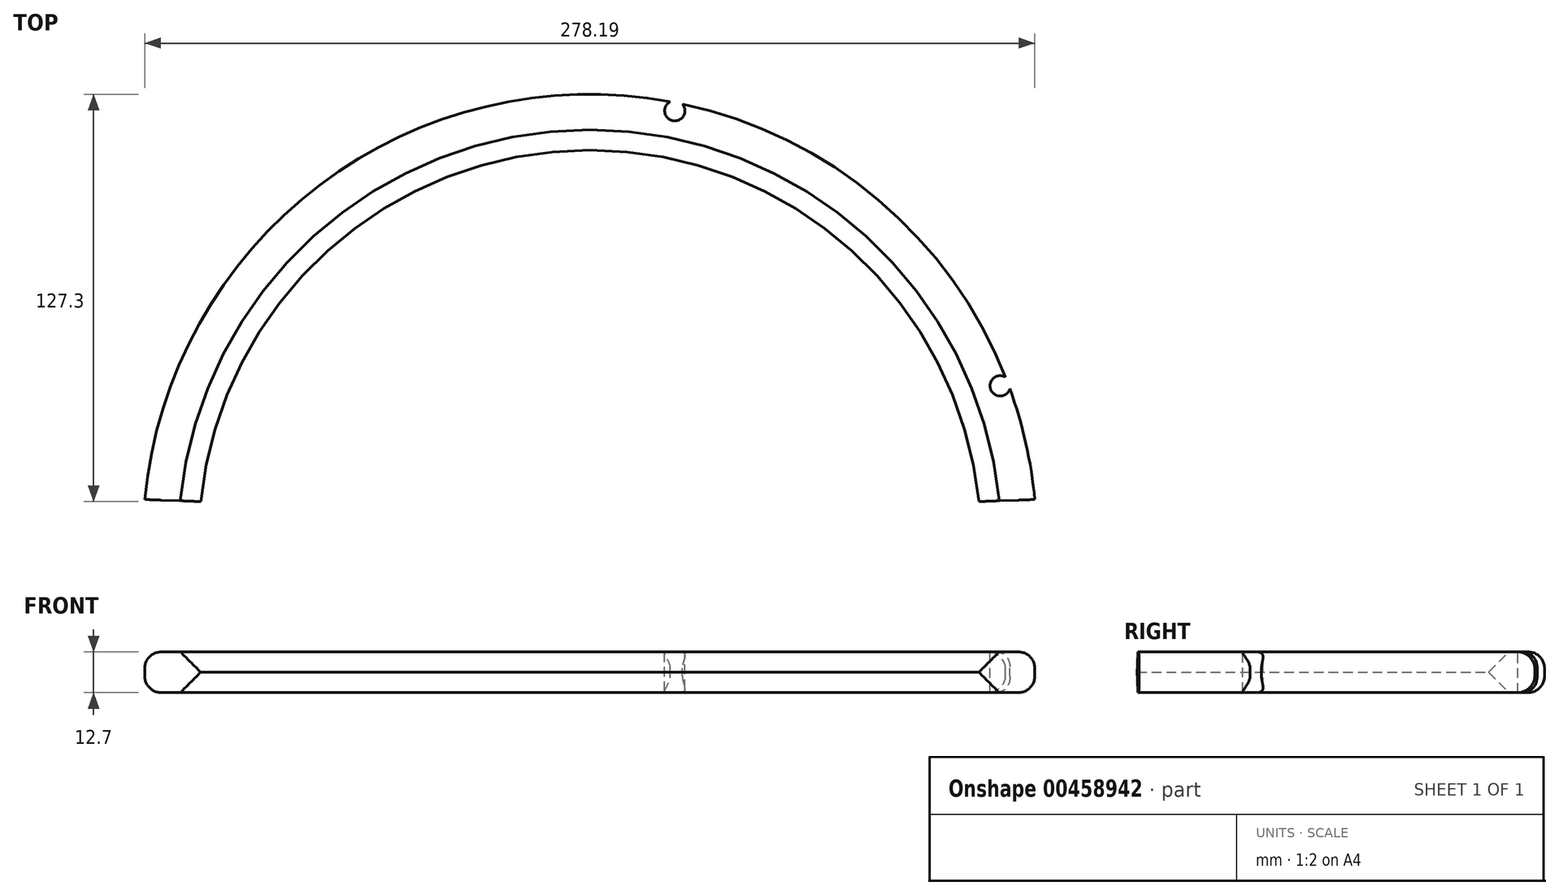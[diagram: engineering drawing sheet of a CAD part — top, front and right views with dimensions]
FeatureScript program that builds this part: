
annotation { "Feature Type Name" : "Feature", "Feature Type Description" : "" }
export const myFeature = defineFeature(function(context is Context, id is Id, definition is map)
    precondition{}
    {
        {
            var Q0;
            Q0=qCreatedBy(makeId("Top.planeOp"),FACE);
            var sketch = newSketch(context, id + "F0", { "sketchPlane" : qUnion([Q0])});
            skArc(sketch, "E0", {"start": v(158.11, 39.99) * mm, "mid": v(36.5, 149.82) * mm, "end": v(-85.1, 39.99) * mm});
            skArc(sketch, "E1", {"start": v(175.6, 40.62) * mm, "mid": v(36.5, 167.29) * mm, "end": v(-102.59, 40.62) * mm});
            skLineSegment(sketch, "E2", {"start": v(-102.59, 40.62) * mm, "end": v(-85.1, 39.99) * mm});
            skLineSegment(sketch, "E3", {"start": v(158.11, 39.99) * mm, "end": v(175.6, 40.62) * mm});
            skSolve(sketch);
        }
        {
            var Q0;
            Q0=makeQuery(id+"F0.imprint","IMPRINT",FACE,{"disambiguationData":[TD([[makeQuery(id+"F0.imprint","IMPRINT",EDGE,{"derivedFrom":sQuery(id+"F0.wireOp",EDGE,"E0")}),-1.0]])]});
            extrude(context, id + "F1", {"entities" : qUnion([Q0]), "depth" : 12.7 * mm});
        }
        {
            var Q0;
            Q0=makeQuery(id+"F1.opExtrude","CAP_EDGE",EDGE,{"disambiguationData":[OSD([sQuery(id+"F0.wireOp",EDGE,"E1")])],"isStart":false});
            var Q1;
            Q1=makeQuery(id+"F1.opExtrude","CAP_EDGE",EDGE,{"disambiguationData":[OSD([sQuery(id+"F0.wireOp",EDGE,"E1")])],"isStart":true});
            fillet(context, id + "F2", {"entities" : qUnion([Q0, Q1]), "radius" : 5.08 * mm, "tangentPropagation" : true, "allowEdgeOverflow" : false});
        }
        {
            var Q0;
            Q0=makeQuery(id+"F1.opExtrude","CAP_EDGE",EDGE,{"disambiguationData":[OSD([sQuery(id+"F0.wireOp",EDGE,"E0")])],"isStart":false});
            var Q1;
            Q1=makeQuery(id+"F1.opExtrude","CAP_EDGE",EDGE,{"disambiguationData":[OSD([sQuery(id+"F0.wireOp",EDGE,"E0")])],"isStart":true});
            chamfer(context, id + "F3", {"entities" : qUnion([Q0, Q1]), "width" : 6.35 * mm, "tangentPropagation" : true});
        }
        {
            var Q0;
            Q0=makeQuery(id+"F1.opExtrude","SWEPT_BODY",BODY,{"disambiguationData":[OSD([sQuery(id+"F0.wireOp",EDGE,"E0"),sQuery(id+"F0.wireOp",EDGE,"E1"),sQuery(id+"F0.wireOp",EDGE,"E2"),sQuery(id+"F0.wireOp",EDGE,"E3")])]});
            var Q1;
            Q1=qCreatedBy(makeId("Top.planeOp"),FACE);
            mirror(context, id + "F4", {"entities" : qUnion([Q0]), "mirrorPlane" : qUnion([Q1])});
        }
        {
            var Q0;
            Q0=makeQuery(id+"F4.opPattern","COPY",BODY,{"derivedFrom":makeQuery(id+"F1.opExtrude","SWEPT_BODY",BODY,{"disambiguationData":[OSD([sQuery(id+"F0.wireOp",EDGE,"E0"),sQuery(id+"F0.wireOp",EDGE,"E1"),sQuery(id+"F0.wireOp",EDGE,"E2"),sQuery(id+"F0.wireOp",EDGE,"E3")])]}),"instanceName":"1"});
            deleteBodies(context, id + "F5", {"entities" : qUnion([Q0])});
        }
        {
            var Q0;
            Q0=makeQuery(id+"F1.opExtrude","CAP_FACE",FACE,{"disambiguationData":[OSD([sQuery(id+"F0.wireOp",EDGE,"E0"),sQuery(id+"F0.wireOp",EDGE,"E1"),sQuery(id+"F0.wireOp",EDGE,"E2"),sQuery(id+"F0.wireOp",EDGE,"E3")])],"isStart":false});
            var sketch = newSketch(context, id + "F6", { "sketchPlane" : qUnion([Q0])});
            skCircle(sketch, "E4", {"center": v(164.78, 76.15) * mm, "radius": 3.18 * mm});
            skSolve(sketch);
        }
        {
            var Q0;
            {var subQ0=sQuery(id+"F6.wireOp",EDGE,"E4");var subQ1=sQuery(id+"F0.wireOp",EDGE,"E1");var subQ2=makeQuery(id+"F2.opFillet","BLEND_EDGE",EDGE,{"blendedFrom":[makeQuery(id+"F1.opExtrude","CAP_EDGE",EDGE,{"disambiguationData":[OSD([subQ1])],"isStart":false}),makeQuery(id+"F1.opExtrude","CAP_FACE",FACE,{"disambiguationData":[OSD([sQuery(id+"F0.wireOp",EDGE,"E0"),subQ1,sQuery(id+"F0.wireOp",EDGE,"E2"),sQuery(id+"F0.wireOp",EDGE,"E3")])],"isStart":false})],"blendedInto":[makeQuery(id+"F1.opExtrude","CAP_FACE",FACE,{"disambiguationData":[OSD([sQuery(id+"F0.wireOp",EDGE,"E0"),subQ1,sQuery(id+"F0.wireOp",EDGE,"E2"),sQuery(id+"F0.wireOp",EDGE,"E3")])],"isStart":false})]});var subQ3=makeQuery(id+"F6.imprint","INTERSECT",VERTEX,{"disambiguationData":[OD(0.0)],"derivedFrom":[subQ2,subQ0]});Q0=makeQuery(id+"F6.imprint","IMPRINT",FACE,{"disambiguationData":[TD([[makeQuery(id+"F6.imprint","IMPRINT",EDGE,{"disambiguationData":[TD([[subQ3,1.0]])],"derivedFrom":subQ0}),1.0]])]});}
            extrude(context, id + "F7", {"entities" : qUnion([Q0]), "operationType" : NewBodyOperationType.REMOVE, "oppositeDirection" : true, "depth" : 25.4 * mm});
        }
        {
            var Q0;
            Q0=makeQuery(id+"F1.opExtrude","CAP_FACE",FACE,{"disambiguationData":[OSD([sQuery(id+"F0.wireOp",EDGE,"E0"),sQuery(id+"F0.wireOp",EDGE,"E1"),sQuery(id+"F0.wireOp",EDGE,"E2"),sQuery(id+"F0.wireOp",EDGE,"E3")])],"isStart":false});
            var sketch = newSketch(context, id + "F8", { "sketchPlane" : qUnion([Q0])});
            skCircle(sketch, "E5", {"center": v(63.07, 162.15) * mm, "radius": 3.18 * mm});
            skSolve(sketch);
        }
        {
            var Q0;
            {var subQ0=sQuery(id+"F8.wireOp",EDGE,"E5");var subQ1=sQuery(id+"F0.wireOp",EDGE,"E2");var subQ2=sQuery(id+"F0.wireOp",EDGE,"E1");var subQ3=makeQuery(id+"F1.opExtrude","CAP_EDGE",EDGE,{"disambiguationData":[OSD([subQ2])],"isStart":false});var subQ4=sQuery(id+"F0.wireOp",EDGE,"E3");var subQ5=sQuery(id+"F0.wireOp",EDGE,"E0");var subQ6=makeQuery(id+"F1.opExtrude","CAP_FACE",FACE,{"disambiguationData":[OSD([subQ5,subQ2,subQ1,subQ4])],"isStart":false});var subQ7=makeQuery(id+"F7.boolean.opBoolean","SPLIT",EDGE,{"disambiguationData":[TD([makeQuery(id+"F1.opExtrude","SWEPT_FACE",FACE,{"disambiguationData":[OSD([subQ1])]})])],"derivedFrom":makeQuery(id+"F2.opFillet","BLEND_EDGE",EDGE,{"blendedFrom":[subQ3,subQ6],"blendedInto":[subQ6]})});var subQ8=makeQuery(id+"F8.imprint","INTERSECT",VERTEX,{"disambiguationData":[OD(0.0)],"derivedFrom":[subQ7,subQ0]});Q0=makeQuery(id+"F8.imprint","IMPRINT",FACE,{"disambiguationData":[TD([[makeQuery(id+"F8.imprint","IMPRINT",EDGE,{"disambiguationData":[TD([[subQ8,1.0]])],"derivedFrom":subQ0}),1.0]])]});}
            var Q1;
            {var subQ0=sQuery(id+"F8.wireOp",EDGE,"E5");var subQ1=sQuery(id+"F0.wireOp",EDGE,"E2");var subQ2=sQuery(id+"F0.wireOp",EDGE,"E1");var subQ3=makeQuery(id+"F1.opExtrude","CAP_EDGE",EDGE,{"disambiguationData":[OSD([subQ2])],"isStart":false});var subQ4=sQuery(id+"F0.wireOp",EDGE,"E3");var subQ5=sQuery(id+"F0.wireOp",EDGE,"E0");var subQ6=makeQuery(id+"F1.opExtrude","CAP_FACE",FACE,{"disambiguationData":[OSD([subQ5,subQ2,subQ1,subQ4])],"isStart":false});var subQ7=makeQuery(id+"F7.boolean.opBoolean","SPLIT",EDGE,{"disambiguationData":[TD([makeQuery(id+"F1.opExtrude","SWEPT_FACE",FACE,{"disambiguationData":[OSD([subQ1])]})])],"derivedFrom":makeQuery(id+"F2.opFillet","BLEND_EDGE",EDGE,{"blendedFrom":[subQ3,subQ6],"blendedInto":[subQ6]})});var subQ8=makeQuery(id+"F8.imprint","INTERSECT",VERTEX,{"disambiguationData":[OD(0.0)],"derivedFrom":[subQ7,subQ0]});Q1=makeQuery(id+"F8.imprint","IMPRINT",FACE,{"disambiguationData":[TD([[makeQuery(id+"F8.imprint","IMPRINT",EDGE,{"disambiguationData":[TD([[subQ8,-1.0]])],"derivedFrom":subQ0}),1.0]])]});}
            extrude(context, id + "F9", {"entities" : qUnion([Q0, Q1]), "operationType" : NewBodyOperationType.REMOVE, "oppositeDirection" : true, "depth" : 25.4 * mm});
        }
        {
            var Q0;
            Q0 = qSketchRegion(id + "F6", true);
            extrude(context, id + "F10", {"entities" : qUnion([Q0]), "operationType" : NewBodyOperationType.REMOVE, "oppositeDirection" : true, "depth" : 25.4 * mm});
        }
    });
